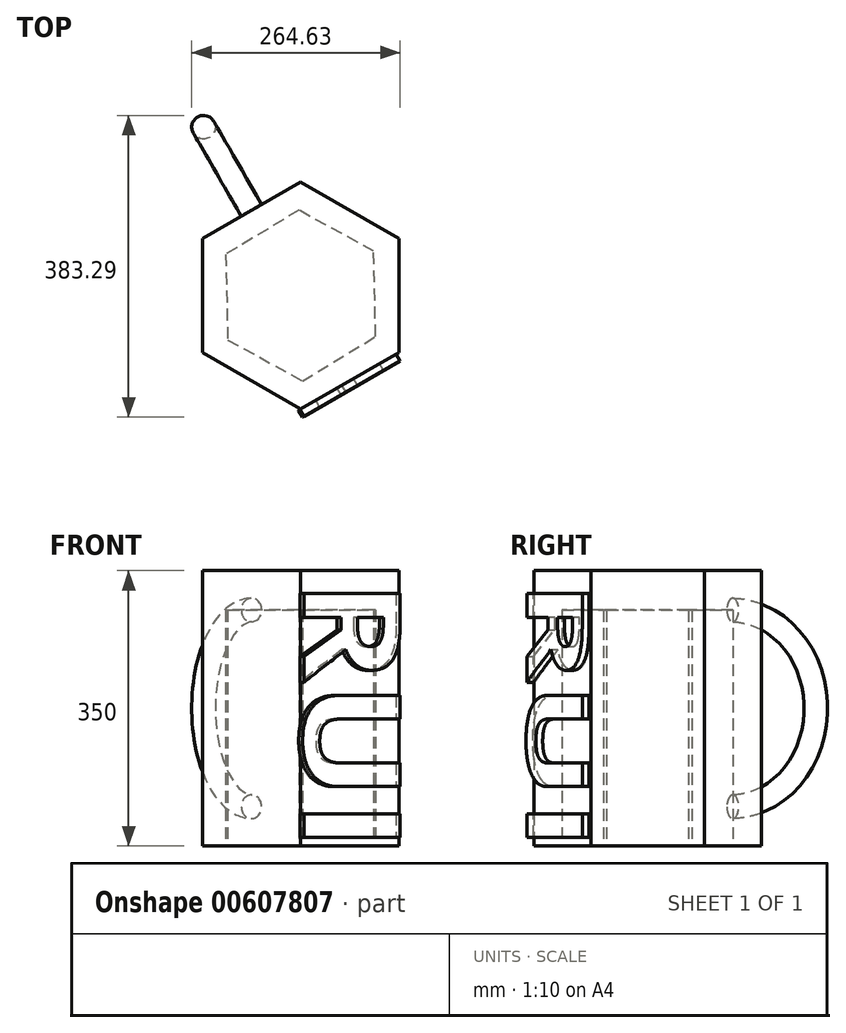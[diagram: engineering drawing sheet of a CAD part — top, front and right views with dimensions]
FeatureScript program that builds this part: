
annotation { "Feature Type Name" : "Feature", "Feature Type Description" : "" }
export const myFeature = defineFeature(function(context is Context, id is Id, definition is map)
    precondition{}
    {
        {
            var Q0;
            Q0=qCreatedBy(makeId("Top.planeOp"),FACE);
            var sketch = newSketch(context, id + "F0", { "sketchPlane" : qUnion([Q0])});
            skCircle(sketch, "E0.cCircle", {"center": v(0, 0) * mm, "radius": 125 * mm, "construction": true});
            skLineSegment(sketch, "E0.0", {"start": v(125, 72.17) * mm, "end": v(125, -72.17) * mm});
            skLineSegment(sketch, "E0.1", {"start": v(125, -72.17) * mm, "end": v(0, -144.34) * mm});
            skLineSegment(sketch, "E0.2", {"start": v(0, -144.34) * mm, "end": v(-125, -72.17) * mm});
            skLineSegment(sketch, "E0.3", {"start": v(-125, -72.17) * mm, "end": v(-125, 72.17) * mm});
            skLineSegment(sketch, "E0.4", {"start": v(-125, 72.17) * mm, "end": v(0, 144.34) * mm});
            skLineSegment(sketch, "E0.5", {"start": v(0, 144.34) * mm, "end": v(125, 72.17) * mm});
            skPoint(sketch, "E0.0.midPoint", {"position": v(125, 0) * mm});
            skSolve(sketch);
        }
        {
            var Q0;
            Q0 = qSketchRegion(id + "F0", true);
            extrude(context, id + "F1", {"entities" : qUnion([Q0]), "depth" : 350 * mm, "offsetDistance" : 25 * mm});
        }
        {
            var Q0;
            Q0=makeQuery(id+"F1.opExtrude","CAP_FACE",FACE,{"disambiguationData":[OSD([sQuery(id+"F0.wireOp",EDGE,"E0.0"),sQuery(id+"F0.wireOp",EDGE,"E0.1"),sQuery(id+"F0.wireOp",EDGE,"E0.2"),sQuery(id+"F0.wireOp",EDGE,"E0.3"),sQuery(id+"F0.wireOp",EDGE,"E0.4"),sQuery(id+"F0.wireOp",EDGE,"E0.5")])],"isStart":false});
            var sketch = newSketch(context, id + "F2", { "sketchPlane" : qUnion([Q0])});
            skCircle(sketch, "E1.cCircle", {"center": v(0, 0) * mm, "radius": 120.68 * mm, "construction": true});
            skLineSegment(sketch, "E1.0", {"start": v(-2.86, 139.32) * mm, "end": v(119.23, 72.14) * mm});
            skLineSegment(sketch, "E1.1", {"start": v(119.23, 72.14) * mm, "end": v(122.1, -67.18) * mm});
            skLineSegment(sketch, "E1.2", {"start": v(122.1, -67.18) * mm, "end": v(2.86, -139.32) * mm});
            skLineSegment(sketch, "E1.3", {"start": v(2.86, -139.32) * mm, "end": v(-119.23, -72.14) * mm});
            skLineSegment(sketch, "E1.4", {"start": v(-119.23, -72.14) * mm, "end": v(-122.1, 67.18) * mm});
            skLineSegment(sketch, "E1.5", {"start": v(-122.1, 67.18) * mm, "end": v(-2.86, 139.32) * mm});
            skPoint(sketch, "E1.0.midPoint", {"position": v(58.18, 105.73) * mm});
            skSolve(sketch);
        }
        {
            var Q0;
            Q0=makeQuery(id+"F1.opExtrude","SWEPT_FACE",FACE,{"disambiguationData":[OSD([sQuery(id+"F0.wireOp",EDGE,"E0.1")])]});
            var sketch = newSketch(context, id + "F3", { "sketchPlane" : qUnion([Q0])});
            skText(sketch, "E2", { "text": "RUI", "fontName": "OpenSans-Bold.ttf"});
            const initialGuessF3  = {"E2": [-0.07318, 0.33843, 0, -1, 0.14214]};
            skSetInitialGuess(sketch, initialGuessF3);
            skSolve(sketch);
        }
        {
            var Q0;
            Q0 = qSketchRegion(id + "F3", true);
            extrude(context, id + "F4", {"entities" : qUnion([Q0]), "operationType" : NewBodyOperationType.ADD, "depth" : 10 * mm, "offsetDistance" : 25 * mm});
        }
        {
            var Q0;
            Q0=makeQuery(id+"F1.opExtrude","CAP_FACE",FACE,{"disambiguationData":[OSD([sQuery(id+"F0.wireOp",EDGE,"E0.0"),sQuery(id+"F0.wireOp",EDGE,"E0.1"),sQuery(id+"F0.wireOp",EDGE,"E0.2"),sQuery(id+"F0.wireOp",EDGE,"E0.3"),sQuery(id+"F0.wireOp",EDGE,"E0.4"),sQuery(id+"F0.wireOp",EDGE,"E0.5")])],"isStart":true});
            var sketch = newSketch(context, id + "F5", { "sketchPlane" : qUnion([Q0])});
            skCircle(sketch, "E3.cCircle", {"center": v(0, 0) * mm, "radius": 94.01 * mm, "construction": true});
            skLineSegment(sketch, "E3.0", {"start": v(-2.42, -108.53) * mm, "end": v(-95.2, -52.16) * mm});
            skLineSegment(sketch, "E3.1", {"start": v(-95.2, -52.16) * mm, "end": v(-92.77, 56.36) * mm});
            skLineSegment(sketch, "E3.2", {"start": v(-92.77, 56.36) * mm, "end": v(2.42, 108.53) * mm});
            skLineSegment(sketch, "E3.3", {"start": v(2.42, 108.53) * mm, "end": v(95.2, 52.16) * mm});
            skLineSegment(sketch, "E3.4", {"start": v(95.2, 52.16) * mm, "end": v(92.77, -56.36) * mm});
            skLineSegment(sketch, "E3.5", {"start": v(92.77, -56.36) * mm, "end": v(-2.42, -108.53) * mm});
            skPoint(sketch, "E3.0.midPoint", {"position": v(-48.81, -80.35) * mm});
            skSolve(sketch);
        }
        {
            var Q0;
            Q0 = qSketchRegion(id + "F5", true);
            extrude(context, id + "F6", {"entities" : qUnion([Q0]), "operationType" : NewBodyOperationType.REMOVE, "oppositeDirection" : true, "depth" : 300 * mm, "offsetDistance" : 25 * mm});
        }
        {
            var Q0;
            Q0=makeQuery(id+"F1.opExtrude","SWEPT_FACE",FACE,{"disambiguationData":[OSD([sQuery(id+"F0.wireOp",EDGE,"E0.4")])]});
            var sketch = newSketch(context, id + "F7", { "sketchPlane" : qUnion([Q0])});
            skCircle(sketch, "E4", {"center": v(0, 50) * mm, "radius": 15 * mm});
            skCircle(sketch, "E5", {"center": v(0, 300) * mm, "radius": 15 * mm});
            skLineSegment(sketch, "E6", {"start": v(0, 0) * mm, "end": v(0, 350) * mm, "construction": true});
            skSolve(sketch);
        }
        {
            var Q0;
            Q0=sQuery(id+"F7.wireOp",EDGE,"E6");
            cPlane(context, id + "F8", {"entities" : qUnion([Q0]), "cplaneType" : CPlaneType.LINE_ANGLE, "offset" : 25 * mm, "angle" : 30 * degree, "width" : 150 * mm, "height" : 150 * mm});
        }
        {
            var Q0;
            Q0=qCreatedBy(id+"F8.planeOp",FACE);
            var sketch = newSketch(context, id + "F9", { "sketchPlane" : qUnion([Q0])});
            skLineSegment(sketch, "E7", {"start": v(121.85, 0) * mm, "end": v(121.85, 350) * mm});
            skPoint(sketch, "E8.endSnap0", {"position": v(121.85, 175) * mm});
            skLineSegment(sketch, "E9", {"start": v(121.85, 300) * mm, "end": v(347.66, 300) * mm, "construction": true});
            skLineSegment(sketch, "E10", {"start": v(121.85, 350) * mm, "end": v(349.19, 350) * mm, "construction": true});
            skLineSegment(sketch, "E11", {"start": v(121.85, 0) * mm, "end": v(324.7, 0) * mm, "construction": true});
            skLineSegment(sketch, "E12", {"start": v(121.85, 50) * mm, "end": v(333.88, 50) * mm, "construction": true});
            skArc(sketch, "E13", {"start": v(121.85, 50) * mm, "mid": v(246.85, 175) * mm, "end": v(121.85, 300) * mm});
            skSolve(sketch);
        }
        {
            var Q0;
            Q0=makeQuery(id+"F7.imprint","IMPRINT",FACE,{"disambiguationData":[TD([[makeQuery(id+"F7.imprint","IMPRINT",EDGE,{"derivedFrom":sQuery(id+"F7.wireOp",EDGE,"E4")}),1.0]])]});
            var Q1;
            Q1=makeQuery(id+"F7.imprint","IMPRINT",FACE,{"disambiguationData":[TD([[makeQuery(id+"F7.imprint","IMPRINT",EDGE,{"derivedFrom":sQuery(id+"F7.wireOp",EDGE,"E5")}),1.0]])]});
            var Q2;
            Q2=sQuery(id+"F9.wireOp",EDGE,"E13");
            sweep(context, id + "F10", {"operationType" : NewBodyOperationType.ADD, "profiles" : qUnion([Q0, Q1]), "path" : qUnion([Q2])});
        }
    });
